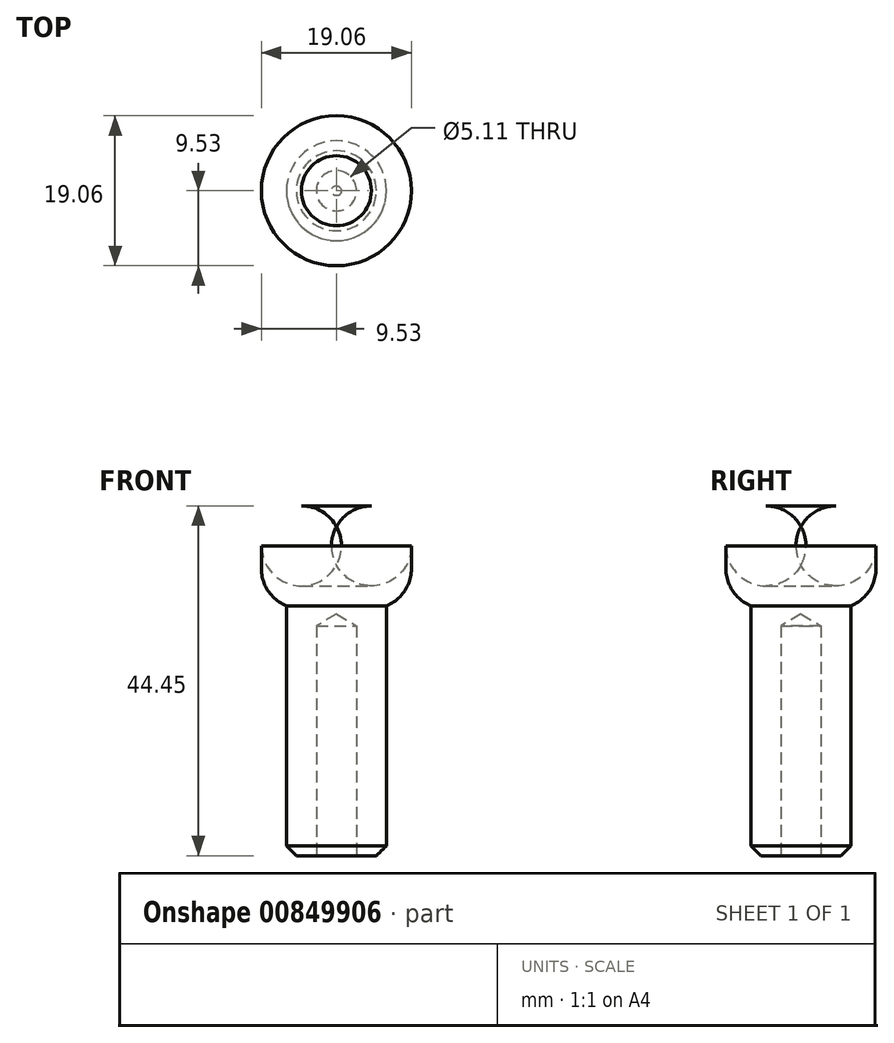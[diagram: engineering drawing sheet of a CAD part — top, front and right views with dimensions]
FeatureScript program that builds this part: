
annotation { "Feature Type Name" : "Feature", "Feature Type Description" : "" }
export const myFeature = defineFeature(function(context is Context, id is Id, definition is map)
    precondition{}
    {
        {
            var Q0;
            Q0=qCreatedBy(makeId("Front.planeOp"),FACE);
            var sketch = newSketch(context, id + "F0", { "sketchPlane" : qUnion([Q0])});
            skLineSegment(sketch, "E0", {"start": v(0, 12.7) * mm, "end": v(9.53, 12.7) * mm});
            skLineSegment(sketch, "E1", {"start": v(9.53, 12.7) * mm, "end": v(9.53, 0) * mm});
            skLineSegment(sketch, "E2", {"start": v(9.53, 0) * mm, "end": v(6.35, 0) * mm});
            skLineSegment(sketch, "E3", {"start": v(6.35, 0) * mm, "end": v(6.35, -31.75) * mm});
            skLineSegment(sketch, "E4", {"start": v(6.35, -31.75) * mm, "end": v(0, -31.75) * mm});
            skLineSegment(sketch, "E5", {"start": v(0, -31.75) * mm, "end": v(0, 12.7) * mm});
            skLineSegment(sketch, "E6", {"start": v(0, 42.92) * mm, "end": v(0, -49.87) * mm, "construction": true});
            skSolve(sketch);
        }
        {
            var Q0;
            Q0=makeQuery(id+"F0.imprint","IMPRINT",FACE,{"disambiguationData":[TD([[makeQuery(id+"F0.imprint","IMPRINT",EDGE,{"derivedFrom":sQuery(id+"F0.wireOp",EDGE,"E0")}),-1.0]])]});
            var Q1;
            Q1=sQuery(id+"F0.wireOp",EDGE,"E6");
            revolve(context, id + "F1", {"surfaceOperationType" : NewSurfaceOperationType.NEW, "entities" : qUnion([Q0]), "axis" : qUnion([Q1]), "revolveType" : RevolveType.FULL, "oppositeDirection" : true});
        }
        {
            var Q0;
            Q0=makeQuery(id+"F1.opRevolve","SWEPT_EDGE",EDGE,{"disambiguationData":[OSD([sQuery(id+"F0.wireOp",EDGE,"E0"),sQuery(id+"F0.wireOp",EDGE,"E1")])]});
            var Q1;
            Q1=makeQuery(id+"F1.opRevolve","SWEPT_EDGE",EDGE,{"disambiguationData":[OSD([sQuery(id+"F0.wireOp",EDGE,"E1"),sQuery(id+"F0.wireOp",EDGE,"E2")])]});
            fillet(context, id + "F2", {"entities" : qUnion([Q0, Q1]), "radius" : 5.08 * mm, "tangentPropagation" : true, "allowEdgeOverflow" : false});
        }
        {
            var Q0;
            Q0=makeQuery(id+"F1.opRevolve","SWEPT_EDGE",EDGE,{"disambiguationData":[OSD([sQuery(id+"F0.wireOp",EDGE,"E3"),sQuery(id+"F0.wireOp",EDGE,"E4")])]});
            chamfer(context, id + "F3", {"entities" : qUnion([Q0]), "width" : 1.27 * mm, "tangentPropagation" : true});
        }
        {
            var Q0;
            Q0=makeQuery(id+"F1.opRevolve","SWEPT_FACE",FACE,{"disambiguationData":[OSD([sQuery(id+"F0.wireOp",EDGE,"E4")])]});
            var sketch = newSketch(context, id + "F4", { "sketchPlane" : qUnion([Q0])});
            skPoint(sketch, "E7", {"position": v(0, 0) * mm});
            skCircle(sketch, "E8", {"center": v(0, 0) * mm, "radius": 4.5 * mm});
            skSolve(sketch);
        }
        {
            var Q0;
            Q0=sQuery(id+"F4.wireOp",VERTEX,"E7");
            var Q1;
            Q1=makeQuery(id+"F1.opRevolve","SWEPT_BODY",BODY,{"disambiguationData":[OSD([sQuery(id+"F0.wireOp",EDGE,"E0"),sQuery(id+"F0.wireOp",EDGE,"E1"),sQuery(id+"F0.wireOp",EDGE,"E2"),sQuery(id+"F0.wireOp",EDGE,"E3"),sQuery(id+"F0.wireOp",EDGE,"E4"),sQuery(id+"F0.wireOp",EDGE,"E5")])]});
            hole(context, id + "F5", {"style" : HoleStyle.SIMPLE, "endStyle" : HoleEndStyle.BLIND, "standardTappedOrClearance" : lookupTablePath({ "standard" : "ANSI", "engagement" : "75%", "pitch" : "20 tpi", "size" : "1/4", "type" : "Tapped" }), "standardBlindInLast" : lookupTablePath({ "standard" : "ANSI", "engagement" : "75%", "pitch" : "20 tpi", "size" : "1/4", "type" : "Tapped" }), "holeDiameter" : 5.1 * mm, "majorDiameter" : 6.35 * mm, "showTappedDepth" : true, "holeDepth" : 29.2 * mm, "isTappedThrough" : true, "tappedDepth" : 25.4 * mm, "tapClearance" : 3, "locations" : qUnion([Q0]), "scope" : qUnion([Q1])});
        }
    });
